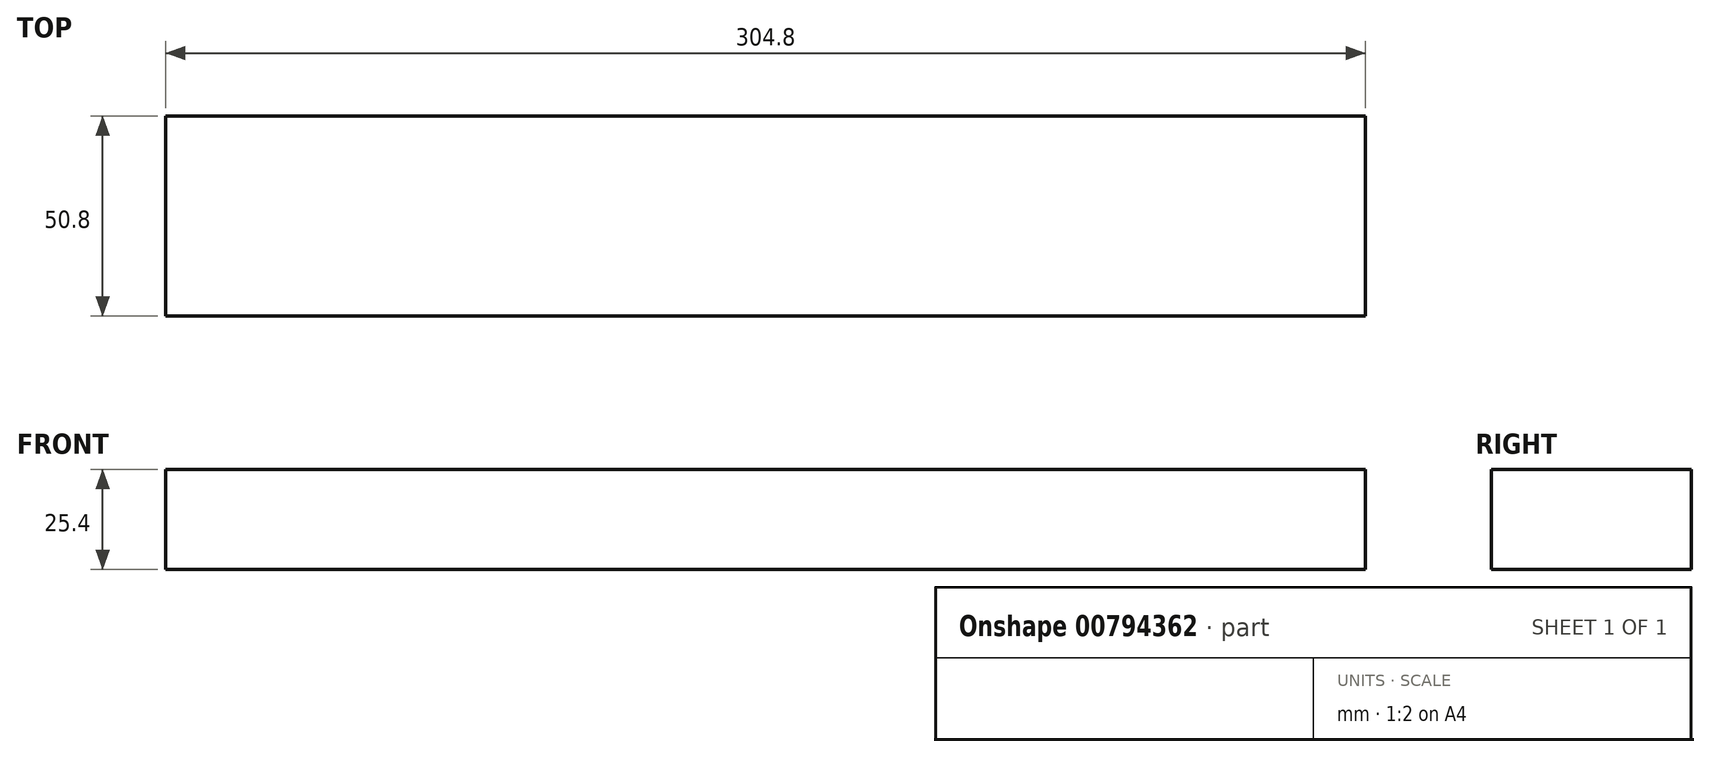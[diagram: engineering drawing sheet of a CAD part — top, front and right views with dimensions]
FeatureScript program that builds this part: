
annotation { "Feature Type Name" : "Feature", "Feature Type Description" : "" }
export const myFeature = defineFeature(function(context is Context, id is Id, definition is map)
    precondition{}
    {
        {
            var Q0;
            Q0=qCreatedBy(makeId("Top.planeOp"),FACE);
            var sketch = newSketch(context, id + "F0", { "sketchPlane" : qUnion([Q0])});
            skLineSegment(sketch, "E0", {"start": v(-43.7, 46.51) * mm, "end": v(-43.7, 33.81) * mm});
            skLineSegment(sketch, "E1", {"start": v(-43.7, 33.81) * mm, "end": v(-43.7, -16.99) * mm});
            skLineSegment(sketch, "E2", {"start": v(-43.7, -16.99) * mm, "end": v(-43.7, -29.69) * mm});
            skLineSegment(sketch, "E3", {"start": v(-43.7, 33.81) * mm, "end": v(261.1, 33.81) * mm});
            skLineSegment(sketch, "E4", {"start": v(261.1, 33.81) * mm, "end": v(261.1, -16.99) * mm});
            skLineSegment(sketch, "E5", {"start": v(-43.7, -16.99) * mm, "end": v(261.1, -16.99) * mm});
            skLineSegment(sketch, "E6", {"start": v(261.1, 33.81) * mm, "end": v(261.1, 46.51) * mm});
            skLineSegment(sketch, "E7", {"start": v(261.1, -16.99) * mm, "end": v(261.1, -29.69) * mm});
            skSolve(sketch);
        }
        {
            var Q0;
            Q0=makeQuery(id+"F0.imprint","IMPRINT",FACE,{"disambiguationData":[TD([[makeQuery(id+"F0.imprint","IMPRINT",EDGE,{"derivedFrom":sQuery(id+"F0.wireOp",EDGE,"E1")}),1.0]])]});
            extrude(context, id + "F1", {"entities" : qUnion([Q0]), "depth" : 25.4 * mm, "offsetDistance" : 25.4 * mm});
        }
    });
